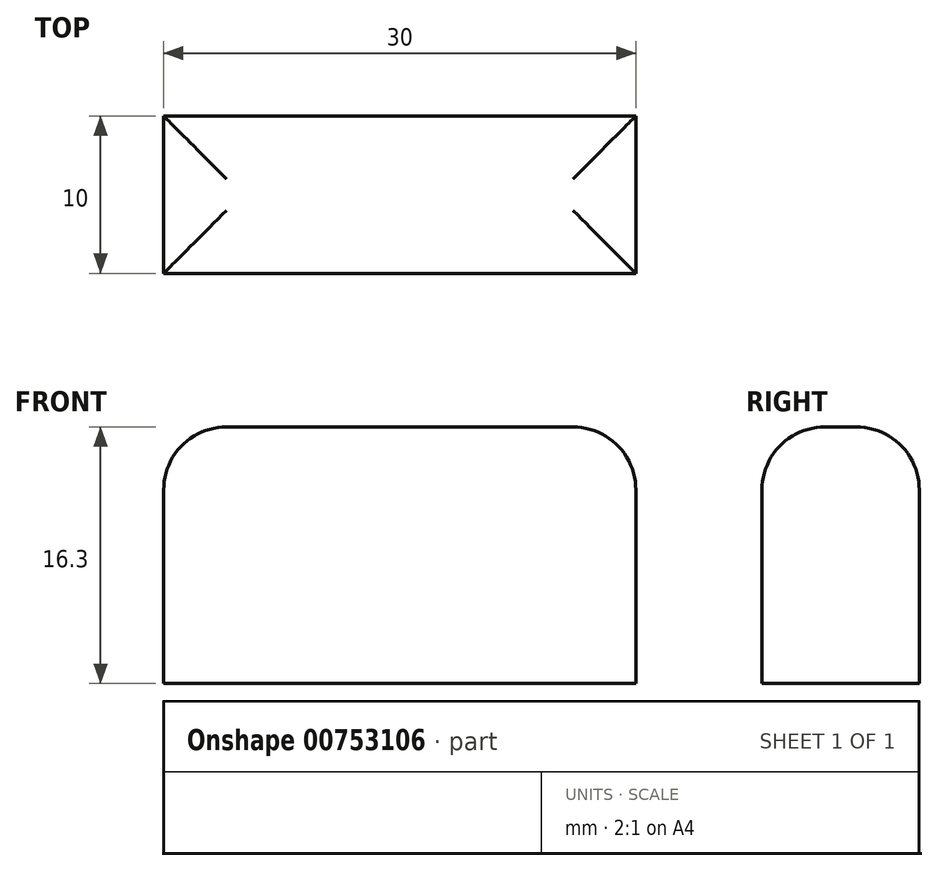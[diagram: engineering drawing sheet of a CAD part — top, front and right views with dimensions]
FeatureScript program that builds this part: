
annotation { "Feature Type Name" : "Feature", "Feature Type Description" : "" }
export const myFeature = defineFeature(function(context is Context, id is Id, definition is map)
    precondition{}
    {
        {
            var Q0;
            Q0=qCreatedBy(makeId("Top.planeOp"),FACE);
            var sketch = newSketch(context, id + "F0", { "sketchPlane" : qUnion([Q0])});
            skLineSegment(sketch, "E0.bottom", {"start": v(-39.85, 15.38) * mm, "end": v(-9.85, 15.38) * mm});
            skLineSegment(sketch, "E0.top", {"start": v(-39.85, 5.38) * mm, "end": v(-9.85, 5.38) * mm});
            skLineSegment(sketch, "E0.left", {"start": v(-39.85, 15.38) * mm, "end": v(-39.85, 5.38) * mm});
            skLineSegment(sketch, "E0.right", {"start": v(-9.85, 15.38) * mm, "end": v(-9.85, 5.38) * mm});
            skSolve(sketch);
        }
        {
            var Q0;
            Q0=makeQuery(id+"F0.imprint","IMPRINT",FACE,{"disambiguationData":[TD([[makeQuery(id+"F0.imprint","IMPRINT",EDGE,{"derivedFrom":sQuery(id+"F0.wireOp",EDGE,"E0.bottom")}),-1.0]])]});
            extrude(context, id + "F1", {"entities" : qUnion([Q0]), "depth" : 16.3 * mm, "offsetDistance" : 25 * mm});
        }
        {
            var Q0;
            Q0=makeQuery(id+"F1.opExtrude","CAP_EDGE",EDGE,{"disambiguationData":[OSD([sQuery(id+"F0.wireOp",EDGE,"E0.top")])],"isStart":false});
            var Q1;
            Q1=makeQuery(id+"F1.opExtrude","CAP_EDGE",EDGE,{"disambiguationData":[OSD([sQuery(id+"F0.wireOp",EDGE,"E0.bottom")])],"isStart":false});
            var Q2;
            Q2=makeQuery(id+"F1.opExtrude","CAP_EDGE",EDGE,{"disambiguationData":[OSD([sQuery(id+"F0.wireOp",EDGE,"E0.left")])],"isStart":false});
            var Q3;
            Q3=makeQuery(id+"F1.opExtrude","CAP_EDGE",EDGE,{"disambiguationData":[OSD([sQuery(id+"F0.wireOp",EDGE,"E0.right")])],"isStart":false});
            fillet(context, id + "F2", {"entities" : qUnion([Q0, Q1, Q2, Q3]), "radius" : 4 * mm, "tangentPropagation" : true, "allowEdgeOverflow" : false});
        }
    });
